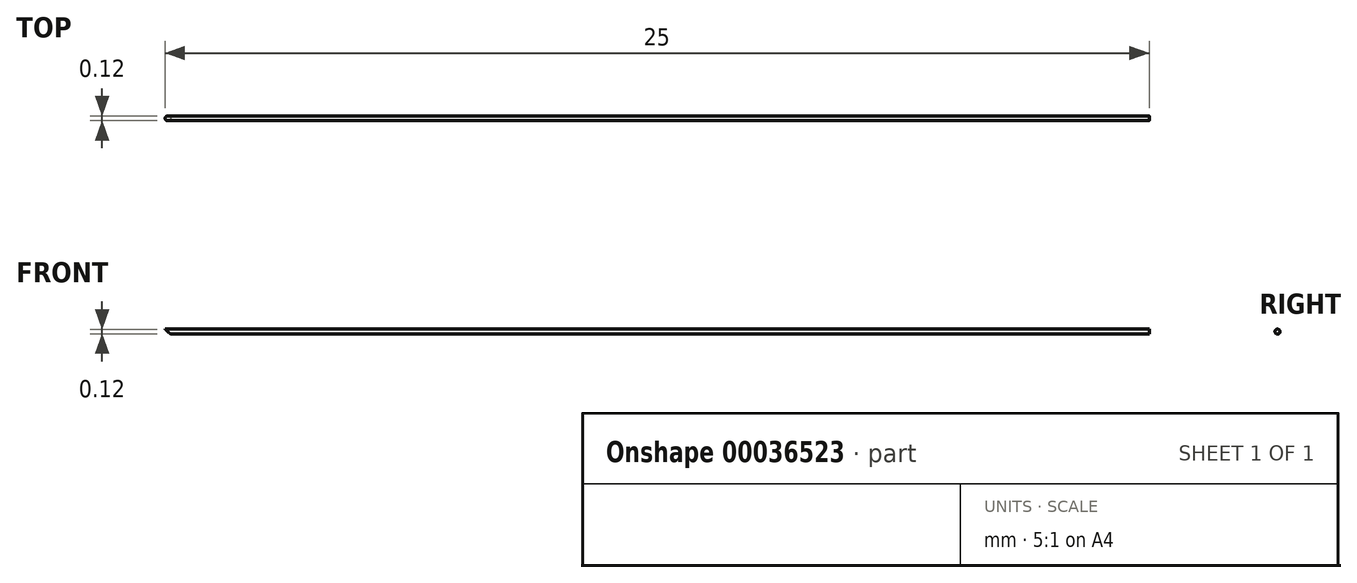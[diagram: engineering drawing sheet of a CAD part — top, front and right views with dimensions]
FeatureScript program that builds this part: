
annotation { "Feature Type Name" : "Feature", "Feature Type Description" : "" }
export const myFeature = defineFeature(function(context is Context, id is Id, definition is map)
    precondition{}
    {
        {
            var Q0;
            Q0=qCreatedBy(makeId("Right.planeOp"),FACE);
            var sketch = newSketch(context, id + "F0", { "sketchPlane" : qUnion([Q0])});
            skCircle(sketch, "E0", {"center": v(0, 0) * mm, "radius": 0.06 * mm});
            skSolve(sketch);
        }
        {
            var Q0;
            Q0 = qSketchRegion(id + "F0", true);
            extrude(context, id + "F1", {"entities" : qUnion([Q0]), "depth" : 25 * mm});
        }
        {
            var Q0;
            Q0=qCreatedBy(makeId("Front.planeOp"),FACE);
            var sketch = newSketch(context, id + "F2", { "sketchPlane" : qUnion([Q0])});
            skLineSegment(sketch, "E1", {"start": v(0, 0.06) * mm, "end": v(0.15, -0.08) * mm});
            skLineSegment(sketch, "E2", {"start": v(0.15, -0.08) * mm, "end": v(0, -0.08) * mm});
            skLineSegment(sketch, "E3", {"start": v(0, -0.08) * mm, "end": v(0, 0.06) * mm});
            skSolve(sketch);
        }
        {
            var Q0;
            Q0 = qSketchRegion(id + "F2", true);
            extrude(context, id + "F3", {"entities" : qUnion([Q0]), "operationType" : NewBodyOperationType.REMOVE, "oppositeDirection" : true, "depth" : 25 * mm});
        }
        {
            var Q0;
            Q0 = qSketchRegion(id + "F2", true);
            extrude(context, id + "F4", {"entities" : qUnion([Q0]), "operationType" : NewBodyOperationType.REMOVE, "depth" : 25 * mm});
        }
    });
